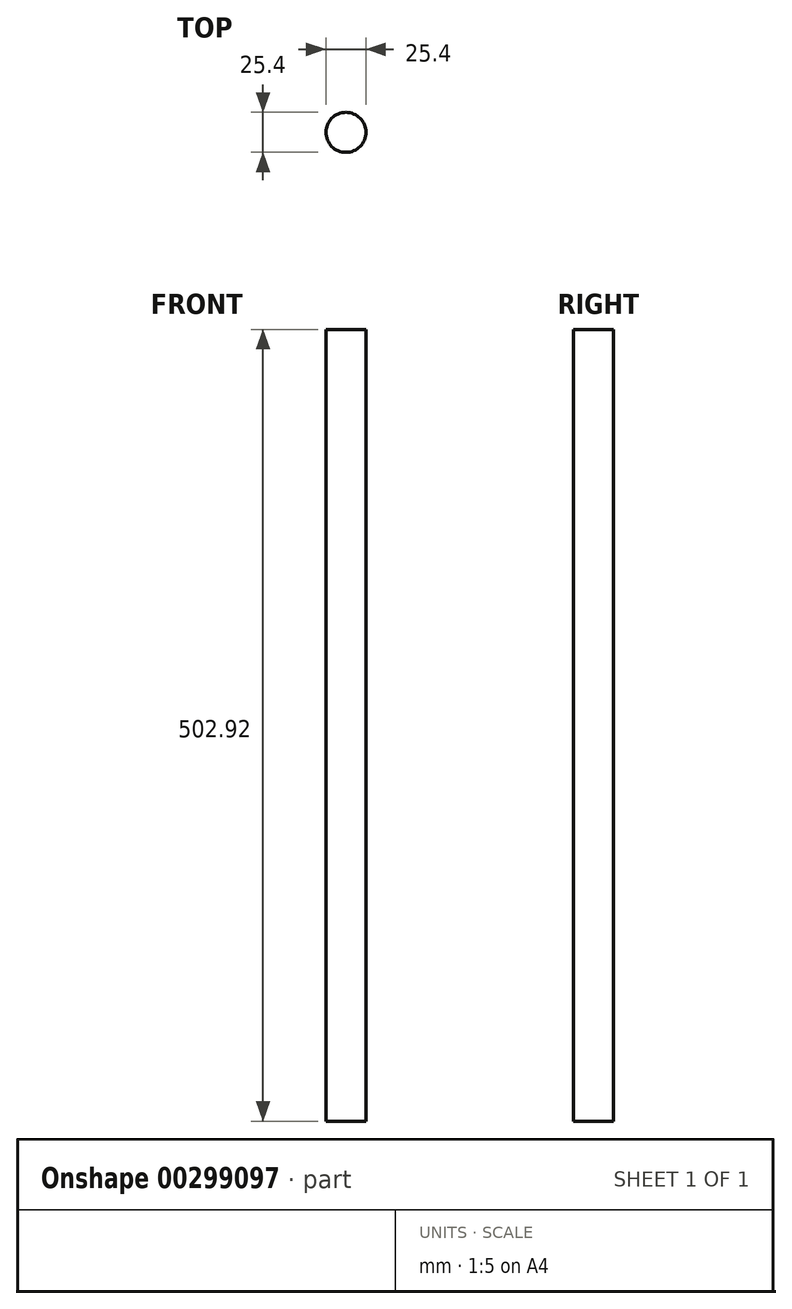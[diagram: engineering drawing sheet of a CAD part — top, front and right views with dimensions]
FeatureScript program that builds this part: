
annotation { "Feature Type Name" : "Feature", "Feature Type Description" : "" }
export const myFeature = defineFeature(function(context is Context, id is Id, definition is map)
    precondition{}
    {
        {
            var Q0;
            Q0=qCreatedBy(makeId("Top.planeOp"),FACE);
            var sketch = newSketch(context, id + "F0", { "sketchPlane" : qUnion([Q0])});
            skCircle(sketch, "E0", {"center": v(0, 0) * mm, "radius": 12.7 * mm});
            skSolve(sketch);
        }
        {
            var Q0;
            Q0 = qSketchRegion(id + "F0", true);
            extrude(context, id + "F1", {"entities" : qUnion([Q0]), "endBound" : BoundingType.SYMMETRIC, "depth" : 502.92 * mm});
        }
    });
